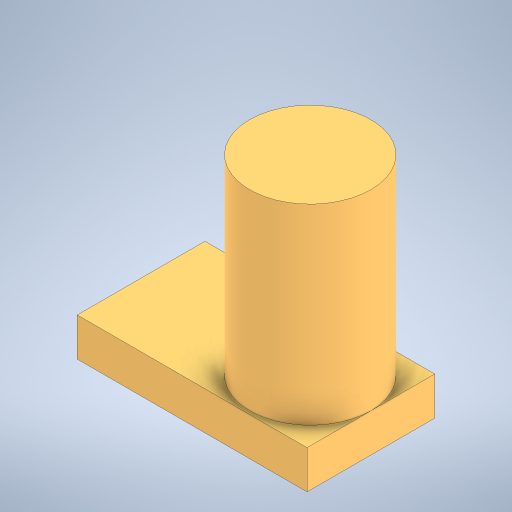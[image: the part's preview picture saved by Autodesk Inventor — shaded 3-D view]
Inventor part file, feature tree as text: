
AUTODESK INVENTOR PART (.ipt)
format: ipt  version: 2024 (Build 280153000, 153)  size: 237,056 bytes
history: native  units: mm
features: extrude x2, sketch x2
ambient origin geometry x8: Origin, YZ Plane, XZ Plane, XY Plane, X Axis, Y Axis, Z Axis, Center Point
bodies: Solid1 (feature_tree)
feature tree (4):
  extrude  "Extrusion1"  Depth=10.0mm
  extrude  "Extrusion2"  Depth=15.0mm
  sketch  "Sketch1"  dims[d0=18.0mm d1=10.0mm]
  sketch  "Sketch2"  dims[d2=3.0mm d3=0.0mm d4=9.5mm d5=15.0mm d6=0.0mm]
